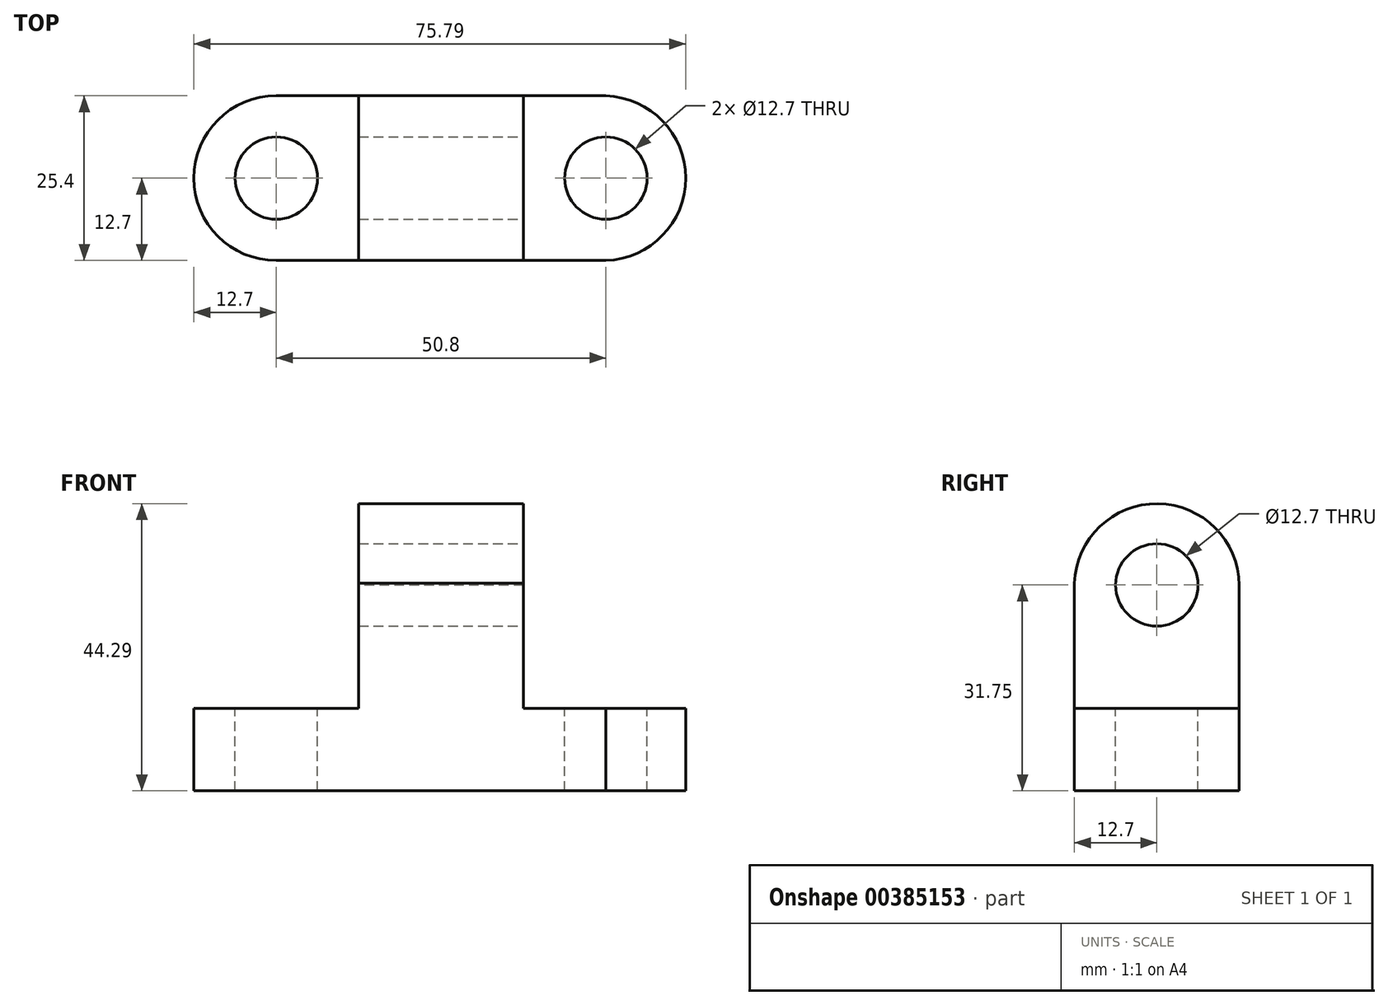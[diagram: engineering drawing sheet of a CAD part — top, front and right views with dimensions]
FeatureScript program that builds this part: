
annotation { "Feature Type Name" : "Feature", "Feature Type Description" : "" }
export const myFeature = defineFeature(function(context is Context, id is Id, definition is map)
    precondition{}
    {
        {
            var Q0;
            Q0=qCreatedBy(makeId("Front.planeOp"),FACE);
            var sketch = newSketch(context, id + "F0", { "sketchPlane" : qUnion([Q0])});
            skLineSegment(sketch, "E0", {"start": v(0, 0) * mm, "end": v(0, 44.45) * mm});
            skLineSegment(sketch, "E1", {"start": v(0, 44.45) * mm, "end": v(76.2, 44.45) * mm});
            skLineSegment(sketch, "E2", {"start": v(76.2, 44.45) * mm, "end": v(76.2, 0) * mm});
            skLineSegment(sketch, "E3", {"start": v(76.2, 0) * mm, "end": v(0, 0) * mm});
            skSolve(sketch);
        }
        {
            var Q0;
            Q0 = qSketchRegion(id + "F0", true);
            extrude(context, id + "F1", {"entities" : qUnion([Q0]), "depth" : 25.4 * mm});
        }
        {
            var Q0;
            Q0=makeQuery(id+"F1.opExtrude","CAP_FACE",FACE,{"disambiguationData":[OSD([sQuery(id+"F0.wireOp",EDGE,"E0"),sQuery(id+"F0.wireOp",EDGE,"E1"),sQuery(id+"F0.wireOp",EDGE,"E2"),sQuery(id+"F0.wireOp",EDGE,"E3")])],"isStart":false});
            var sketch = newSketch(context, id + "F2", { "sketchPlane" : qUnion([Q0])});
            skLineSegment(sketch, "E4", {"start": v(50.8, 44.45) * mm, "end": v(50.8, 12.7) * mm});
            skLineSegment(sketch, "E5", {"start": v(50.8, 12.7) * mm, "end": v(76.2, 12.7) * mm});
            skLineSegment(sketch, "E6", {"start": v(25.4, 44.45) * mm, "end": v(25.4, 12.7) * mm});
            skLineSegment(sketch, "E7", {"start": v(25.4, 12.7) * mm, "end": v(0, 12.7) * mm});
            skSolve(sketch);
        }
        {
            var Q0;
            {var subQ0=sQuery(id+"F2.wireOp",EDGE,"E6");Q0=makeQuery(id+"F2.imprint","IMPRINT",FACE,{"disambiguationData":[TD([[makeQuery(id+"F2.imprint","IMPRINT",EDGE,{"derivedFrom":subQ0}),-1.0]])]});}
            var Q1;
            {var subQ0=sQuery(id+"F2.wireOp",EDGE,"E4");Q1=makeQuery(id+"F2.imprint","IMPRINT",FACE,{"disambiguationData":[TD([[makeQuery(id+"F2.imprint","IMPRINT",EDGE,{"derivedFrom":subQ0}),1.0]])]});}
            extrude(context, id + "F3", {"entities" : qUnion([Q0, Q1]), "operationType" : NewBodyOperationType.REMOVE, "oppositeDirection" : true, "depth" : 25.4 * mm});
        }
        {
            var Q0;
            Q0=makeQuery(id+"F3.boolean.opBoolean","COPY",FACE,{"derivedFrom":makeQuery(id+"F3.opExtrude","SWEPT_FACE",FACE,{"disambiguationData":[OSD([sQuery(id+"F2.wireOp",EDGE,"E4")])]})});
            var sketch = newSketch(context, id + "F4", { "sketchPlane" : qUnion([Q0])});
            skCircle(sketch, "E8", {"center": v(-12.7, 31.75) * mm, "radius": 6.35 * mm});
            skSolve(sketch);
        }
        {
            var Q0;
            Q0=makeQuery(id+"F4.imprint","IMPRINT",FACE,{"disambiguationData":[TD([[makeQuery(id+"F4.imprint","IMPRINT",EDGE,{"derivedFrom":sQuery(id+"F4.wireOp",EDGE,"E8")}),1.0]])]});
            extrude(context, id + "F5", {"entities" : qUnion([Q0]), "operationType" : NewBodyOperationType.REMOVE, "oppositeDirection" : true, "depth" : 25.4 * mm});
        }
        {
            var Q0;
            Q0=makeQuery(id+"F3.boolean.opBoolean","COPY",FACE,{"derivedFrom":makeQuery(id+"F3.opExtrude","SWEPT_FACE",FACE,{"disambiguationData":[OSD([sQuery(id+"F2.wireOp",EDGE,"E5")])]})});
            var sketch = newSketch(context, id + "F6", { "sketchPlane" : qUnion([Q0])});
            skCircle(sketch, "E9", {"center": v(12.7, -12.7) * mm, "radius": 6.35 * mm});
            skCircle(sketch, "E10", {"center": v(63.5, -12.7) * mm, "radius": 6.35 * mm});
            skSolve(sketch);
        }
        {
            var Q0;
            Q0=makeQuery(id+"F6.imprint","IMPRINT",FACE,{"disambiguationData":[TD([[makeQuery(id+"F6.imprint","IMPRINT",EDGE,{"derivedFrom":sQuery(id+"F6.wireOp",EDGE,"E9")}),1.0]])]});
            var Q1;
            Q1=makeQuery(id+"F6.imprint","IMPRINT",FACE,{"disambiguationData":[TD([[makeQuery(id+"F6.imprint","IMPRINT",EDGE,{"derivedFrom":sQuery(id+"F6.wireOp",EDGE,"E10")}),1.0]])]});
            extrude(context, id + "F7", {"entities" : qUnion([Q0, Q1]), "operationType" : NewBodyOperationType.REMOVE, "oppositeDirection" : true, "depth" : 25.4 * mm});
        }
        {
            var Q0;
            Q0=makeQuery(id+"F3.boolean.opBoolean","COPY",FACE,{"derivedFrom":makeQuery(id+"F3.opExtrude","SWEPT_FACE",FACE,{"disambiguationData":[OSD([sQuery(id+"F2.wireOp",EDGE,"E7")])]})});
            var sketch = newSketch(context, id + "F8", { "sketchPlane" : qUnion([Q0])});
            skArc(sketch, "E11", {"start": v(12.7, 0) * mm, "mid": v(0, -12.7) * mm, "end": v(12.7, -25.4) * mm});
            skSolve(sketch);
        }
        {
            var Q0;
            {var subQ0=sQuery(id+"F8.wireOp",EDGE,"E11");var subQ1=sQuery(id+"F2.wireOp",EDGE,"E7");var subQ2=makeQuery(id+"F3.boolean.opBoolean","COPY",EDGE,{"derivedFrom":makeQuery(id+"F3.opExtrude","CAP_EDGE",EDGE,{"disambiguationData":[OSD([subQ1])],"isStart":false})});var subQ3=makeQuery(id+"F8.imprint","INTERSECT",VERTEX,{"derivedFrom":[subQ2,subQ0]});Q0=makeQuery(id+"F8.imprint","IMPRINT",FACE,{"disambiguationData":[TD([[makeQuery(id+"F8.imprint","IMPRINT",EDGE,{"disambiguationData":[TD([[subQ3,-1.0]])],"derivedFrom":subQ0}),-1.0]])]});}
            var Q1;
            {var subQ0=sQuery(id+"F8.wireOp",EDGE,"E11");var subQ1=sQuery(id+"F2.wireOp",EDGE,"E7");var subQ2=makeQuery(id+"F3.boolean.opBoolean","COPY",EDGE,{"derivedFrom":makeQuery(id+"F3.opExtrude","CAP_EDGE",EDGE,{"disambiguationData":[OSD([subQ1])],"isStart":true})});var subQ3=makeQuery(id+"F8.imprint","INTERSECT",VERTEX,{"derivedFrom":[subQ2,subQ0]});Q1=makeQuery(id+"F8.imprint","IMPRINT",FACE,{"disambiguationData":[TD([[makeQuery(id+"F8.imprint","IMPRINT",EDGE,{"disambiguationData":[TD([[subQ3,1.0]])],"derivedFrom":subQ0}),-1.0]])]});}
            extrude(context, id + "F9", {"entities" : qUnion([Q0, Q1]), "operationType" : NewBodyOperationType.REMOVE, "oppositeDirection" : true, "depth" : 25.4 * mm});
        }
        {
            var Q0;
            Q0=makeQuery(id+"F3.boolean.opBoolean","COPY",FACE,{"derivedFrom":makeQuery(id+"F3.opExtrude","SWEPT_FACE",FACE,{"disambiguationData":[OSD([sQuery(id+"F2.wireOp",EDGE,"E5")])]})});
            var sketch = newSketch(context, id + "F10", { "sketchPlane" : qUnion([Q0])});
            skArc(sketch, "E12", {"start": v(63.5, -25.4) * mm, "mid": v(75.79, -12.7) * mm, "end": v(63.5, 0) * mm});
            skSolve(sketch);
        }
        {
            var Q0;
            {var subQ0=sQuery(id+"F10.wireOp",EDGE,"E12");Q0=makeQuery(id+"F10.imprint","IMPRINT",FACE,{"disambiguationData":[TD([[makeQuery(id+"F10.imprint","IMPRINT",EDGE,{"derivedFrom":subQ0}),-1.0]])]});}
            extrude(context, id + "F11", {"entities" : qUnion([Q0]), "operationType" : NewBodyOperationType.REMOVE, "oppositeDirection" : true, "depth" : 25.4 * mm});
        }
        {
            var Q0;
            Q0=makeQuery(id+"F3.boolean.opBoolean","COPY",FACE,{"derivedFrom":makeQuery(id+"F3.opExtrude","SWEPT_FACE",FACE,{"disambiguationData":[OSD([sQuery(id+"F2.wireOp",EDGE,"E6")])]})});
            var sketch = newSketch(context, id + "F12", { "sketchPlane" : qUnion([Q0])});
            skArc(sketch, "E13", {"start": v(25.4, 32.03) * mm, "mid": v(12.55, 44.28) * mm, "end": v(0, 31.73) * mm});
            skSolve(sketch);
        }
        {
            var Q0;
            {var subQ0=sQuery(id+"F12.wireOp",EDGE,"E13");Q0=makeQuery(id+"F12.imprint","IMPRINT",FACE,{"disambiguationData":[TD([[makeQuery(id+"F12.imprint","IMPRINT",EDGE,{"derivedFrom":subQ0}),-1.0]])]});}
            extrude(context, id + "F13", {"entities" : qUnion([Q0]), "operationType" : NewBodyOperationType.REMOVE, "oppositeDirection" : true, "depth" : 25.4 * mm});
        }
    });
